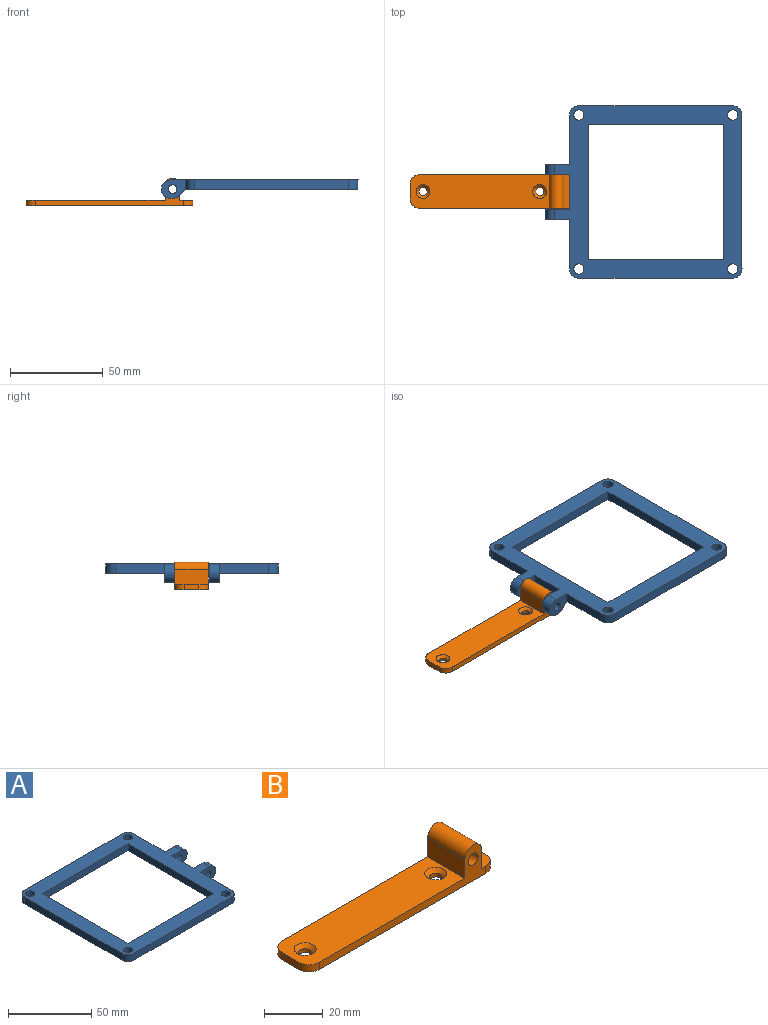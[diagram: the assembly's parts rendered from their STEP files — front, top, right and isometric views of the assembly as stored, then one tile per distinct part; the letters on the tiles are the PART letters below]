
ASSEMBLY  parts=2 mates=1
PART A: 34 faces, bbox 106x93x10 mm
  f0: plane 26.5x5mm, normal (1,0,0), area 132.5mm2, adj f14,f15,f21,f32
  f1: plane 26.5x5mm, normal (1,0,0), area 132.5mm2, adj f14,f15,f18,f33
  f2: plane 83x5mm, normal (0,1,0), area 415mm2, adj f14,f15,f30,f33
  f3: plane 83x5mm, normal (-1,0,0), area 415mm2, adj f14,f15,f30,f31
  f4: plane 83x5mm, normal (0,-1,0), area 415mm2, adj f14,f15,f31,f32
  f5: plane 73x5mm, normal (1,0,0), area 365mm2, adj f6,f8,f14,f15
  f6: plane 73x5mm, normal (0,-1,0), area 365mm2, adj f5,f7,f14,f15
  f7: plane 73x5mm, normal (-1,0,0), area 365mm2, adj f6,f8,f14,f15
  f8: plane 73x5mm, normal (0,1,0), area 365mm2, adj f5,f7,f14,f15
  f9: cylinder r=2.75mm len=5.5mm, axis (0,0,-1), area 86.4mm2, adj f14,f15
  f10: cylinder r=2.75mm len=5.5mm, axis (0,0,-1), area 86.4mm2, adj f14,f15
  f11: cylinder r=2.75mm len=5.5mm, axis (0,0,-1), area 86.4mm2, adj f14,f15
  f12: cylinder r=2.75mm len=5.5mm, axis (0,0,-1), area 86.4mm2, adj f14,f15
  f13: plane 18.5x5mm, normal (1,0,0), area 92.5mm2, adj f14,f15,f16,f20
  f14: plane 101x93mm, normal (0,0,1), area 3295.5mm2, adj f0,f1,f2,f3,f4,f5,f6,f7
  f15: plane 93x93mm, normal (0,0,-1), area 3203.5mm2, adj f0,f1,f2,f3,f4,f5,f6,f7
  f16: plane 13x10mm, normal (0,-1,0), area 88.1mm2, adj f13,f14,f17,f23,f24,f27,f28
  f17: plane 5.75x0.93mm, normal (0,0,-1), area 5.3mm2, adj f16,f18,f27,f28
  f18: plane 13x10mm, normal (0,1,0), area 88.1mm2, adj f1,f14,f17,f23,f24,f27,f28
  f19: plane 5.75x0.93mm, normal (0,0,-1), area 5.3mm2, adj f20,f21,f26,f29
  f20: plane 13x10mm, normal (0,1,0), area 88.1mm2, adj f13,f14,f19,f22,f25,f26,f29
  f21: plane 13x10mm, normal (0,-1,0), area 88.1mm2, adj f0,f14,f19,f22,f25,f26,f29
  f22: cylinder r=2.4mm len=5.75mm, axis (0,1,0), area 86.7mm2, adj f20,f21
  f23: cylinder r=2.4mm len=5.75mm, axis (0,1,0), area 86.7mm2, adj f16,f18
  f24: plane 5.75x3.54mm, normal (-0.71,0,-0.71), area 28.8mm2, adj f15,f16,f18,f27
  f25: plane 5.75x3.54mm, normal (-0.71,0,-0.71), area 28.8mm2, adj f15,f20,f21,f26
  f26: cylinder r=5mm len=5.75mm, axis (0,1,0), area 22.6mm2, adj f19,f20,f21,f25
  f27: cylinder r=5mm len=5.75mm, axis (0,1,0), area 22.6mm2, adj f16,f17,f18,f24
  f28: cylinder r=5mm len=10mm, axis (0,-1,0), area 90.3mm2, adj f14,f16,f17,f18
  f29: cylinder r=5mm len=10mm, axis (0,-1,0), area 90.3mm2, adj f14,f19,f20,f21
  f30: cylinder r=5mm len=5mm, axis (0,0,1), area 39.3mm2, adj f2,f3,f14,f15
  f31: cylinder r=5mm len=5mm, axis (0,0,-1), area 39.3mm2, adj f3,f4,f14,f15
  f32: cylinder r=5mm len=5mm, axis (0,0,1), area 39.3mm2, adj f0,f4,f14,f15
  f33: cylinder r=5mm len=5mm, axis (0,0,-1), area 39.3mm2, adj f1,f2,f14,f15
PART B: 19 faces, bbox 90x18x15 mm
  f0: plane 18x7mm, normal (0,0,1), area 115.3mm2, adj f1,f3,f6,f9,f17,f18
  f1: plane 80x15mm, normal (0,1,0), area 311mm2, adj f0,f7,f8,f9,f10,f11,f14,f15
  f2: plane 8x3mm, normal (-1,0,0), area 24mm2, adj f7,f8,f15,f16
  f3: plane 80x15mm, normal (0,-1,0), area 311mm2, adj f0,f7,f8,f9,f10,f11,f14,f16
  f4: cylinder r=2.25mm len=4.5mm, axis (0,0,-1), area 21.2mm2, adj f8,f13
  f5: cylinder r=2.25mm len=4.5mm, axis (0,0,-1), area 21.2mm2, adj f8,f12
  f6: plane 8x3mm, normal (1,0,0), area 24mm2, adj f0,f8,f17,f18
  f7: plane 75x18mm, normal (0,0,1), area 1250.9mm2, adj f1,f2,f3,f10,f12,f13,f15,f16
  f8: plane 90x18mm, normal (0,0,-1), area 1566.7mm2, adj f1,f2,f3,f4,f5,f6,f15,f16
  f9: plane 18x8mm, normal (1,0,0), area 144mm2, adj f0,f1,f3,f14
  f10: plane 18x8mm, normal (-1,0,0), area 144mm2, adj f1,f3,f7,f14
  f11: cylinder r=2.4mm len=18mm, axis (0,1,0), area 271.4mm2, adj f1,f3
  f12: cone r=2.25mm half-angle=45deg, axis (0,0,1), area 40mm2, adj f5,f7
  f13: cone r=2.25mm half-angle=45deg, axis (0,0,1), area 40mm2, adj f4,f7
  f14: cylinder r=4mm len=18mm, axis (0,-1,0), area 226.2mm2, adj f1,f3,f9,f10
  f15: cylinder r=5mm len=5mm, axis (0,0,1), area 23.6mm2, adj f1,f2,f7,f8
  f16: cylinder r=5mm len=5mm, axis (0,0,-1), area 23.6mm2, adj f2,f3,f7,f8
  f17: cylinder r=5mm len=5mm, axis (0,0,1), area 23.6mm2, adj f0,f3,f6,f8
  f18: cylinder r=5mm len=5mm, axis (0,0,-1), area 23.6mm2, adj f0,f1,f6,f8
PLACE A rot(axis=(0,0,-1),180deg) t=(142.16,47.27,-2.71)mm
PLACE B rot(axis=(0.07,0.04,1),0deg) t=(46.56,-17.84,-11.71)mm
MATE revolute A.f22 <-> B.f11  axis (0,-1,0) through (83.88,-8.84,-2.71)mm
